# Revit family: IS_Strada_K0813_BIM_DE
name_source: partatom
category: Plumbing Fixtures
revit_build: Autodesk Revit MEP 2016 (Build: 20161004_0715(x64)
units: mm (PartAtom-declared; Revit-internal decimal feet)

## family parameters
Always vertical = No
Cut with Voids When Loaded = No
OmniClass Number = 23.45.05.14.14
OmniClass Title = Sinks/Lavatories
Part Type = Normal
Room Calculation Point = No
Round Connector Dimension = Use Diameter
Shared = No
Work Plane-Based = No

## types (2) — shared parameters
Accessories = www.idealstandard.de\ersatzteile
AreaUnits = millimeters
AssetType = Fixed
BIMobject category = Basins
BOSUseNativeGeometries = 1
Brand = Ideal Standard
Brand url = http://www.idealstandard.de
CodePerformance = DIN EN 14688 CL 20, DIN EN 31
ConnectionType = Plumbing
CurrencyUnit = €
DurationUnit = year
EAN code = https://4015413058599
Edition number = 1
ExpectedLife = 25
Features = STRADA washbasin 710x420mm, no taphole, with overflow
IFC Classification = Sanitary Terminal
IfcExportAs = WASHHANDBASIN
IfcExportType = Sanitary Terminal
Installation instructions = http://www.idealstandard.de
InstallationInstructions = www.idealstandard.de\produkte
LinearUnits = millimeters
Manufacturer name = Ideal Standard
ManufacturerURL = http://www.idealstandard.de
Material = Vitreous china
Material main = Ceramics
NBS Reference Code = 35-79-94
NBS Reference Description = Wall-Hung Wash Basins
NettWeight = 15 kg
Nominal height = 145
Nominal width = 710
NominalDepth = 420 mm  [stored 1.37795 ft]
NominalHeight = 130 mm  [stored 0.426509 ft]
NominalLength = 420 mm  [stored 1.37795 ft]
NominalWidth = 700 mm  [stored 2.29659 ft]
OmniClass Code = 23-31 13 00
OmniClass Description = Sinks
Product Guid = 628acdbd-6177-4cf2-a922-b6b45e897b59
Product SKU = K0813
Product certification = DIN EN 14688 CL 20, DIN EN 31
Product data url = https://bimobject.com
Product family = STRADA
Product group = Basin
Product name = STRADA washbasin 710x420mm, no taphole, with overflow
Product url = http://www.idealstandard.de
ProductInformation = http://www.idealstandard.de
QR code = http://bimobject.com
Shape = Sculptured
Size = 700x420x130 mm
Space = Internal
SpareParts = www.idealstandard.de/ersatzteile
Technical description = http://www.idealstandard.de
Uniclass 1.4 Code = L7212
Uniclass 1.4 Description = Washbasins
Uniclass 2.0 Code = PR-35-79-94
Uniclass 2.0 Description = Wall-Hung Wash Basins
Uniclass 2015 Code = Pr_40_20_96_96
Uniclass 2015 Name = Wall-hung wash basins
Uniclass2015Code = Pr_40_20_96_96
Uniclass2015Title = Wall-hung wash basins
Uniclass2015Version = Products v1.1
Version = 1
VolumeUnits = Litres
WashHandBasinMounting = WallHung
WashHandBasinType = HANDRINSE
Weight Net (Kg) = 15
zero-valued in all types: DrainSize

## per-type parameters (varying)
| type | BarCode | Color | Finish | MainColor | Model | ModelNumber |
| K081301 STRADA washbasin 710x420mm, no taphole, with overflow | 4015413058599 | White | White | White | K081301 | K081301 |
| K0813MA STRADA washbasin 710x420mm, no taphole, with overflow | 4015413058650 | WHITE IP | WHITE IP | WHITE IP | K0813MA | K0813MA |

note: column(s) folded — value = type name in every type: Description, ModelReference

note: [stored X ft] marks values corroborated as IEEE doubles in the binary element streams (Revit-internal decimal feet)

## geometry (parser evidence)
native form markers: Blend x4
no freeform markers — native parametric forms only
